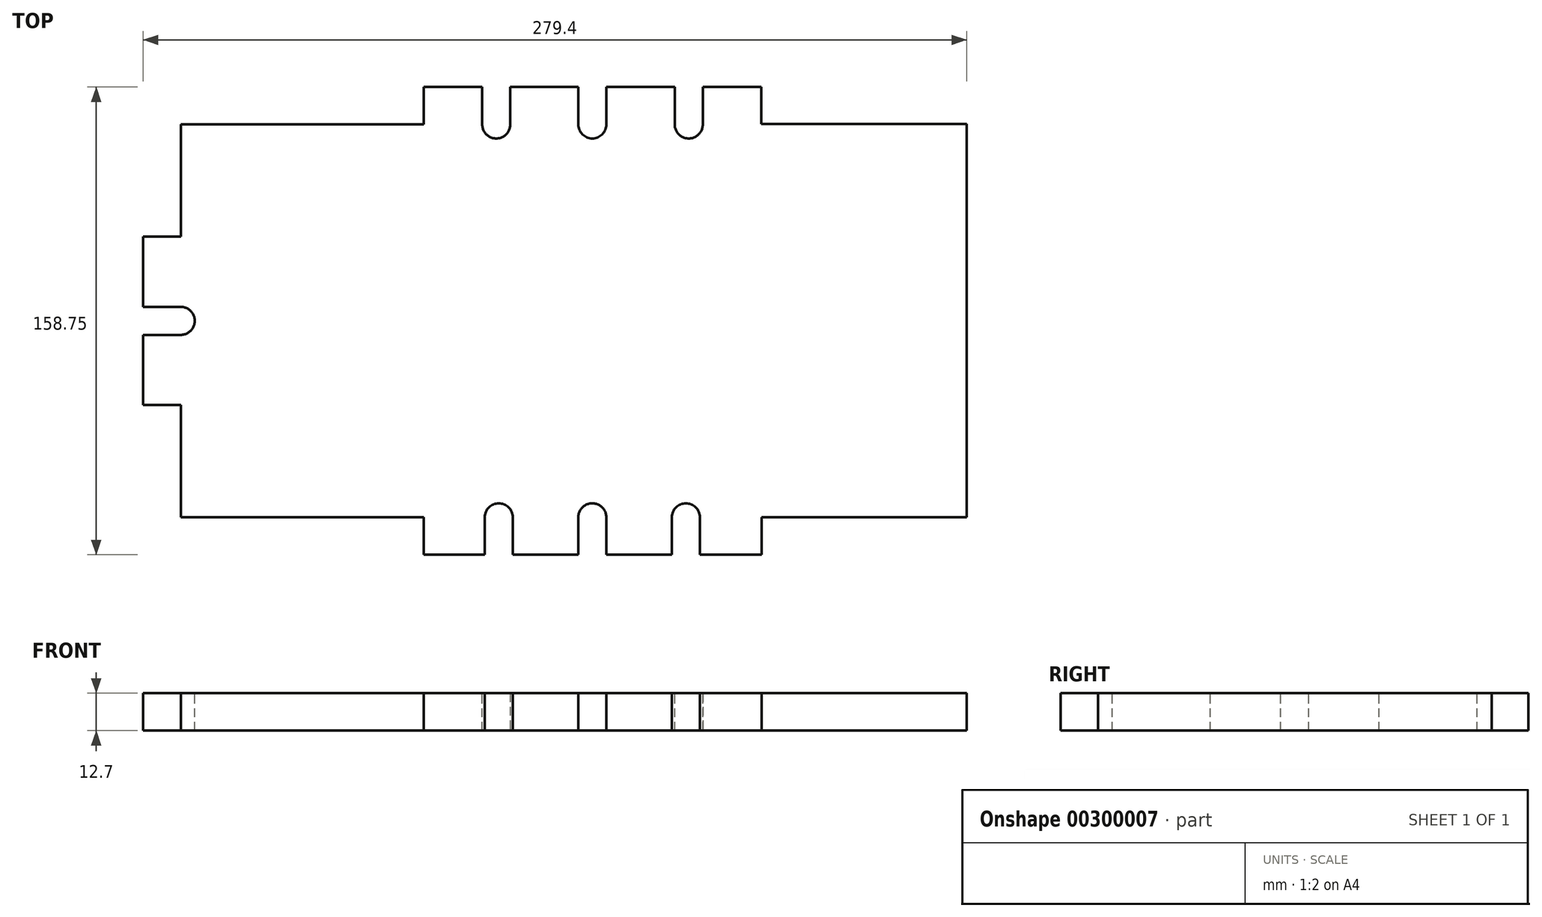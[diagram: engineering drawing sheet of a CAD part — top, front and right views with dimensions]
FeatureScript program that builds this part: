
annotation { "Feature Type Name" : "Feature", "Feature Type Description" : "" }
export const myFeature = defineFeature(function(context is Context, id is Id, definition is map)
    precondition{}
    {
        {
            var Q0;
            Q0=qCreatedBy(makeId("Top.planeOp"),FACE);
            var sketch = newSketch(context, id + "F0", { "sketchPlane" : qUnion([Q0])});
            skLineSegment(sketch, "E0.bottom", {"start": v(0, 0) * mm, "end": v(279.4, 0) * mm});
            skLineSegment(sketch, "E0.top", {"start": v(0, 158.75) * mm, "end": v(279.4, 158.75) * mm});
            skLineSegment(sketch, "E0.left", {"start": v(0, 0) * mm, "end": v(0, 158.75) * mm});
            skLineSegment(sketch, "E0.right", {"start": v(279.4, 0) * mm, "end": v(279.4, 158.75) * mm});
            skSolve(sketch);
        }
        {
            var Q0;
            Q0 = qSketchRegion(id + "F0", true);
            extrude(context, id + "F1", {"entities" : qUnion([Q0]), "oppositeDirection" : true, "depth" : 12.7 * mm});
        }
        {
            var Q0;
            Q0=qCreatedBy(makeId("Top.planeOp"),FACE);
            var sketch = newSketch(context, id + "F2", { "sketchPlane" : qUnion([Q0])});
            skLineSegment(sketch, "E1.bottom", {"start": v(0, 158.82) * mm, "end": v(12.7, 158.82) * mm});
            skLineSegment(sketch, "E1.top", {"start": v(0, 108.02) * mm, "end": v(12.7, 108.02) * mm});
            skLineSegment(sketch, "E1.left", {"start": v(0, 158.82) * mm, "end": v(0, 108.02) * mm});
            skLineSegment(sketch, "E1.right", {"start": v(12.7, 158.82) * mm, "end": v(12.7, 108.02) * mm});
            skPoint(sketch, "E2.oppositeSnap0", {"position": v(12.7, 133.42) * mm});
            skLineSegment(sketch, "E2.bottom", {"start": v(0, 0) * mm, "end": v(12.7, 0) * mm});
            skLineSegment(sketch, "E2.top", {"start": v(0, 50.8) * mm, "end": v(12.7, 50.8) * mm});
            skLineSegment(sketch, "E2.left", {"start": v(0, 0) * mm, "end": v(0, 50.8) * mm});
            skLineSegment(sketch, "E2.right", {"start": v(12.7, 0) * mm, "end": v(12.7, 50.8) * mm});
            skSolve(sketch);
        }
        {
            var Q0;
            Q0=makeQuery(id+"F2.imprint","IMPRINT",FACE,{"disambiguationData":[TD([[makeQuery(id+"F2.imprint","IMPRINT",EDGE,{"derivedFrom":sQuery(id+"F2.wireOp",EDGE,"E1.bottom")}),-1.0]])]});
            var Q1;
            Q1=makeQuery(id+"F2.imprint","IMPRINT",FACE,{"disambiguationData":[TD([[makeQuery(id+"F2.imprint","IMPRINT",EDGE,{"derivedFrom":sQuery(id+"F2.wireOp",EDGE,"E2.bottom")}),1.0]])]});
            extrude(context, id + "F3", {"entities" : qUnion([Q0, Q1]), "operationType" : NewBodyOperationType.REMOVE, "endBound" : BoundingType.THROUGH_ALL, "oppositeDirection" : true, "depth" : 25.4 * mm});
        }
        {
            var Q0;
            Q0=qCreatedBy(makeId("Top.planeOp"),FACE);
            var sketch = newSketch(context, id + "F4", { "sketchPlane" : qUnion([Q0])});
            skArc(sketch, "E3", {"start": v(12.7, 74.61) * mm, "mid": v(17.46, 79.43) * mm, "end": v(12.6, 84.14) * mm});
            skLineSegment(sketch, "E4", {"start": v(12.6, 84.14) * mm, "end": v(0, 84.14) * mm});
            skLineSegment(sketch, "E5", {"start": v(12.7, 74.61) * mm, "end": v(0, 74.61) * mm});
            skLineSegment(sketch, "E6", {"start": v(0, 84.14) * mm, "end": v(0, 74.61) * mm});
            skSolve(sketch);
        }
        {
            var Q0;
            Q0=makeQuery(id+"F4.imprint","IMPRINT",FACE,{"disambiguationData":[TD([[makeQuery(id+"F4.imprint","IMPRINT",EDGE,{"derivedFrom":sQuery(id+"F4.wireOp",EDGE,"E3")}),1.0]])]});
            extrude(context, id + "F5", {"entities" : qUnion([Q0]), "operationType" : NewBodyOperationType.REMOVE, "endBound" : BoundingType.THROUGH_ALL, "oppositeDirection" : true, "depth" : 25.4 * mm});
        }
        {
            var Q0;
            Q0=qCreatedBy(makeId("Top.planeOp"),FACE);
            var sketch = newSketch(context, id + "F6", { "sketchPlane" : qUnion([Q0])});
            skLineSegment(sketch, "E7.bottom", {"start": v(12.61, 158.85) * mm, "end": v(95.16, 158.85) * mm});
            skLineSegment(sketch, "E7.top", {"start": v(12.61, 146.15) * mm, "end": v(95.16, 146.15) * mm});
            skLineSegment(sketch, "E7.left", {"start": v(12.61, 158.85) * mm, "end": v(12.61, 146.15) * mm});
            skLineSegment(sketch, "E7.right", {"start": v(95.16, 158.85) * mm, "end": v(95.16, 146.15) * mm});
            skLineSegment(sketch, "E8.bottom", {"start": v(12.67, 0) * mm, "end": v(95.22, 0) * mm});
            skLineSegment(sketch, "E8.top", {"start": v(12.67, 12.7) * mm, "end": v(95.22, 12.7) * mm});
            skLineSegment(sketch, "E8.left", {"start": v(12.67, 0) * mm, "end": v(12.67, 12.7) * mm});
            skLineSegment(sketch, "E8.right", {"start": v(95.22, 0) * mm, "end": v(95.22, 12.7) * mm});
            skLineSegment(sketch, "E9.bottom", {"start": v(279.53, 158.9) * mm, "end": v(209.68, 158.9) * mm});
            skLineSegment(sketch, "E9.top", {"start": v(279.53, 146.2) * mm, "end": v(209.68, 146.2) * mm});
            skLineSegment(sketch, "E9.left", {"start": v(279.53, 158.9) * mm, "end": v(279.53, 146.2) * mm});
            skLineSegment(sketch, "E9.right", {"start": v(209.68, 158.9) * mm, "end": v(209.68, 146.2) * mm});
            skLineSegment(sketch, "E10.bottom", {"start": v(279.67, 0) * mm, "end": v(209.82, 0) * mm});
            skLineSegment(sketch, "E10.top", {"start": v(279.67, 12.7) * mm, "end": v(209.82, 12.7) * mm});
            skLineSegment(sketch, "E10.left", {"start": v(279.67, 0) * mm, "end": v(279.67, 12.7) * mm});
            skLineSegment(sketch, "E10.right", {"start": v(209.82, 0) * mm, "end": v(209.82, 12.7) * mm});
            skSolve(sketch);
        }
        {
            var Q0;
            Q0=makeQuery(id+"F6.imprint","IMPRINT",FACE,{"disambiguationData":[TD([[makeQuery(id+"F6.imprint","IMPRINT",EDGE,{"derivedFrom":sQuery(id+"F6.wireOp",EDGE,"E10.bottom")}),-1.0]])]});
            var Q1;
            Q1=makeQuery(id+"F6.imprint","IMPRINT",FACE,{"disambiguationData":[TD([[makeQuery(id+"F6.imprint","IMPRINT",EDGE,{"derivedFrom":sQuery(id+"F6.wireOp",EDGE,"E8.bottom")}),1.0]])]});
            var Q2;
            Q2=makeQuery(id+"F6.imprint","IMPRINT",FACE,{"disambiguationData":[TD([[makeQuery(id+"F6.imprint","IMPRINT",EDGE,{"derivedFrom":sQuery(id+"F6.wireOp",EDGE,"E7.bottom")}),-1.0]])]});
            var Q3;
            Q3=makeQuery(id+"F6.imprint","IMPRINT",FACE,{"disambiguationData":[TD([[makeQuery(id+"F6.imprint","IMPRINT",EDGE,{"derivedFrom":sQuery(id+"F6.wireOp",EDGE,"E9.bottom")}),1.0]])]});
            extrude(context, id + "F7", {"entities" : qUnion([Q0, Q1, Q2, Q3]), "operationType" : NewBodyOperationType.REMOVE, "endBound" : BoundingType.THROUGH_ALL, "oppositeDirection" : true, "depth" : 25.4 * mm});
        }
        {
            var Q0;
            Q0=qCreatedBy(makeId("Top.planeOp"),FACE);
            var sketch = newSketch(context, id + "F8", { "sketchPlane" : qUnion([Q0])});
            skArc(sketch, "E11", {"start": v(157.16, 12.54) * mm, "mid": v(152.47, 17.46) * mm, "end": v(147.64, 12.67) * mm});
            skArc(sketch, "E12", {"start": v(147.64, 146.05) * mm, "mid": v(152.4, 141.29) * mm, "end": v(157.16, 146.05) * mm});
            skLineSegment(sketch, "E13", {"start": v(147.64, 12.73) * mm, "end": v(147.64, 0) * mm});
            skLineSegment(sketch, "E14", {"start": v(157.16, 12.54) * mm, "end": v(157.16, 0) * mm});
            skLineSegment(sketch, "E15", {"start": v(147.64, 0) * mm, "end": v(157.16, 0) * mm});
            skLineSegment(sketch, "E16", {"start": v(157.16, 146.05) * mm, "end": v(157.16, 158.79) * mm});
            skLineSegment(sketch, "E17", {"start": v(157.16, 158.79) * mm, "end": v(147.63, 158.79) * mm});
            skLineSegment(sketch, "E18", {"start": v(147.63, 158.79) * mm, "end": v(147.64, 146.05) * mm});
            skArc(sketch, "E19", {"start": v(125.41, 12.7) * mm, "mid": v(120.65, 17.46) * mm, "end": v(115.89, 12.7) * mm});
            skArc(sketch, "E20", {"start": v(188.91, 12.7) * mm, "mid": v(184.15, 17.46) * mm, "end": v(179.39, 12.7) * mm});
            skLineSegment(sketch, "E21", {"start": v(115.89, 12.7) * mm, "end": v(115.89, 0) * mm});
            skLineSegment(sketch, "E22", {"start": v(125.41, 12.7) * mm, "end": v(125.41, 0) * mm});
            skLineSegment(sketch, "E23", {"start": v(125.41, 0) * mm, "end": v(115.89, 0) * mm});
            skLineSegment(sketch, "E24", {"start": v(179.39, 12.7) * mm, "end": v(179.39, 0) * mm});
            skLineSegment(sketch, "E25", {"start": v(188.91, 12.7) * mm, "end": v(188.91, 0) * mm});
            skLineSegment(sketch, "E26", {"start": v(188.91, 0) * mm, "end": v(179.39, 0) * mm});
            skArc(sketch, "E27", {"start": v(180.36, 146.05) * mm, "mid": v(185.13, 141.29) * mm, "end": v(189.89, 146.05) * mm});
            skArc(sketch, "E28", {"start": v(115.03, 146.05) * mm, "mid": v(119.8, 141.29) * mm, "end": v(124.56, 146.05) * mm});
            skLineSegment(sketch, "E29", {"start": v(115.03, 146.05) * mm, "end": v(115.04, 158.75) * mm});
            skLineSegment(sketch, "E30", {"start": v(124.56, 146.05) * mm, "end": v(124.56, 158.75) * mm});
            skLineSegment(sketch, "E31", {"start": v(124.56, 158.75) * mm, "end": v(115.04, 158.75) * mm});
            skLineSegment(sketch, "E32", {"start": v(189.89, 146.05) * mm, "end": v(189.89, 158.75) * mm});
            skLineSegment(sketch, "E33", {"start": v(180.36, 146.05) * mm, "end": v(180.36, 158.75) * mm});
            skLineSegment(sketch, "E34", {"start": v(180.36, 158.75) * mm, "end": v(189.89, 158.75) * mm});
            skSolve(sketch);
        }
        {
            var Q0;
            Q0=makeQuery(id+"F8.imprint","IMPRINT",FACE,{"disambiguationData":[TD([[makeQuery(id+"F8.imprint","IMPRINT",EDGE,{"derivedFrom":sQuery(id+"F8.wireOp",EDGE,"E12")}),1.0]])]});
            var Q1;
            {var subQ6=sQuery(id+"F8.wireOp",EDGE,"E14");Q1=makeQuery(id+"F8.imprint","IMPRINT",FACE,{"disambiguationData":[TD([[makeQuery(id+"F8.imprint","IMPRINT",EDGE,{"derivedFrom":subQ6}),-1.0]])]});}
            extrude(context, id + "F9", {"entities" : qUnion([Q0, Q1]), "operationType" : NewBodyOperationType.REMOVE, "endBound" : BoundingType.THROUGH_ALL, "oppositeDirection" : true, "depth" : 25.4 * mm});
        }
        {
            var Q0;
            {var subQ6=sQuery(id+"F8.wireOp",EDGE,"E14");Q0=makeQuery(id+"F8.imprint","IMPRINT",FACE,{"disambiguationData":[TD([[makeQuery(id+"F8.imprint","IMPRINT",EDGE,{"derivedFrom":subQ6}),-1.0]])]});}
            var Q1;
            Q1=makeQuery(id+"F8.imprint","IMPRINT",FACE,{"disambiguationData":[TD([[makeQuery(id+"F8.imprint","IMPRINT",EDGE,{"derivedFrom":sQuery(id+"F8.wireOp",EDGE,"E20")}),1.0]])]});
            var Q2;
            Q2=makeQuery(id+"F8.imprint","IMPRINT",FACE,{"disambiguationData":[TD([[makeQuery(id+"F8.imprint","IMPRINT",EDGE,{"derivedFrom":sQuery(id+"F8.wireOp",EDGE,"E19")}),1.0]])]});
            var Q3;
            Q3=makeQuery(id+"F8.imprint","IMPRINT",FACE,{"disambiguationData":[TD([[makeQuery(id+"F8.imprint","IMPRINT",EDGE,{"derivedFrom":sQuery(id+"F8.wireOp",EDGE,"E28")}),1.0]])]});
            var Q4;
            Q4=makeQuery(id+"F8.imprint","IMPRINT",FACE,{"disambiguationData":[TD([[makeQuery(id+"F8.imprint","IMPRINT",EDGE,{"derivedFrom":sQuery(id+"F8.wireOp",EDGE,"E12")}),1.0]])]});
            var Q5;
            Q5=makeQuery(id+"F8.imprint","IMPRINT",FACE,{"disambiguationData":[TD([[makeQuery(id+"F8.imprint","IMPRINT",EDGE,{"derivedFrom":sQuery(id+"F8.wireOp",EDGE,"E27")}),1.0]])]});
            extrude(context, id + "F10", {"entities" : qUnion([Q0, Q1, Q2, Q3, Q4, Q5]), "operationType" : NewBodyOperationType.REMOVE, "endBound" : BoundingType.THROUGH_ALL, "oppositeDirection" : true, "depth" : 25.4 * mm});
        }
    });
